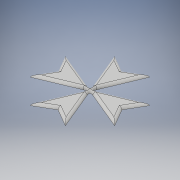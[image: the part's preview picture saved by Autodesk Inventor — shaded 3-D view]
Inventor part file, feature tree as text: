
AUTODESK INVENTOR PART (.ipt)
format: ipt  version: 2019 (Build 230136000, 136)  size: 208,384 bytes
history: native  units: mm
features: extrude x3, sketch x3, fillet x1
ambient origin geometry x8: Origin, YZ Plane, XZ Plane, XY Plane, X Axis, Y Axis, Z Axis, Center Point
bodies: Solid1 (feature_tree)
feature tree (7):
  extrude  "Extrusion1"  TaperAngle=67.5deg  [1 undecoded]
  extrude  "Extrusion2"  TaperAngle=22.5deg  [1 undecoded]
  fillet  "Fillet3"  [1 undecoded]
  extrude  "Extrusion4"  TaperAngle=157.5deg  [1 undecoded]
  sketch  "Sketch1"  dims[d1=112.5deg d2=67.5deg]
  sketch  "Sketch2"  dims[d3=22.5deg d4=22.5deg d5=67.5deg]
  sketch  "Sketch4"  dims[d6=112.5deg d7=157.5deg d8=157.5deg d9=2.0mm d10=0.0mm d11=2.0mm d12=0.0mm d17=0.3mm d18=1.7mm d19=0.0mm]
note: 4 required parameter values undecoded (feature->parameter linkage not recoverable at this tier; creation-order binding heuristic only, values carry confidence <= 0.55)
